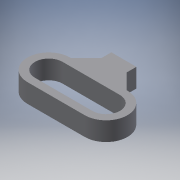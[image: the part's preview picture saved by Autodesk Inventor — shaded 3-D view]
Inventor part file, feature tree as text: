
AUTODESK INVENTOR PART (.ipt)
format: ipt  version: 2017 (Build 210142000, 142)  size: 126,464 bytes
history: native  units: mm
features: extrude x2, sketch x2, chamfer x1
ambient origin geometry x8: Origin, YZ Plane, XZ Plane, XY Plane, X Axis, Y Axis, Z Axis, Center Point
bodies: Solid1 (feature_tree)
feature tree (5):
  extrude  "Extrusion1"  Depth=6.0mm
  extrude  "Extrusion2"  Depth=20.0mm
  chamfer  "Chamfer1"  Distance=20.0mm
  sketch  "Sketch1"  dims[d0=22.0mm d1=6.0mm]
  sketch  "Sketch2"  dims[d2=45.72mm d3=20.0mm d4=20.0mm d5=15.0mm d6=0.0mm d7=7.0mm d8=15.0mm d9=0.0mm d10=12.25mm d11=2.0mm d12=45.0deg]
